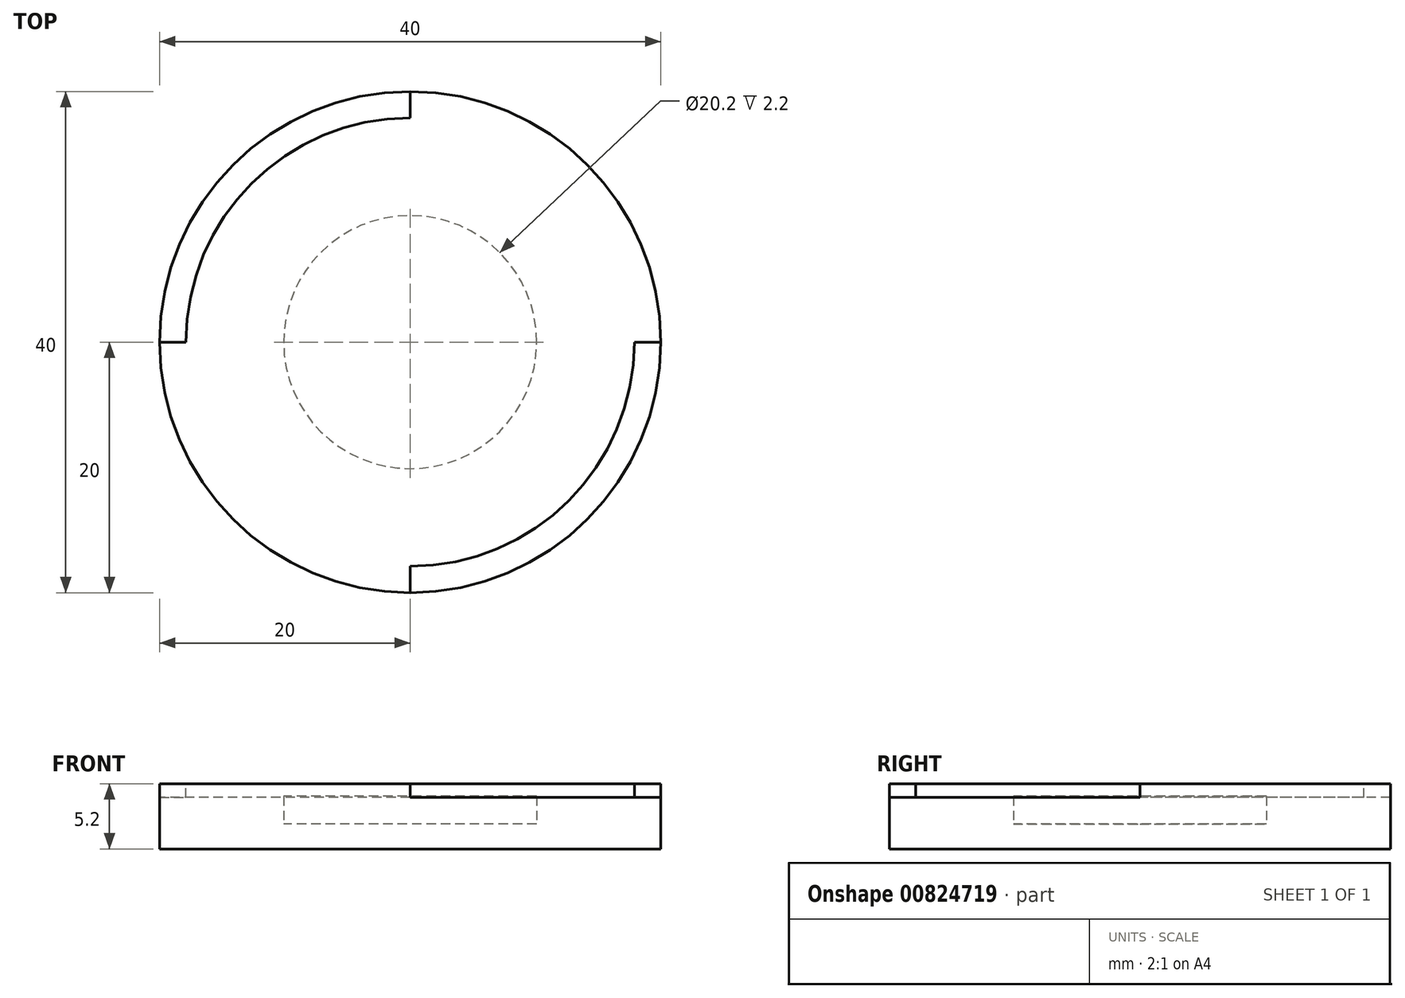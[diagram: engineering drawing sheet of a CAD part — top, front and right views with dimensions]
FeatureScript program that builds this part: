
annotation { "Feature Type Name" : "Feature", "Feature Type Description" : "" }
export const myFeature = defineFeature(function(context is Context, id is Id, definition is map)
    precondition{}
    {
        {
            var Q0;
            Q0=qCreatedBy(makeId("Top.planeOp"),FACE);
            var sketch = newSketch(context, id + "F0", { "sketchPlane" : qUnion([Q0])});
            skCircle(sketch, "E0", {"center": v(0, 0) * mm, "radius": 20 * mm});
            skCircle(sketch, "E1", {"center": v(0, 0) * mm, "radius": 10.1 * mm});
            skSolve(sketch);
        }
        {
            var Q0;
            Q0=makeQuery(id+"F0.imprint","IMPRINT",FACE,{"disambiguationData":[TD([[makeQuery(id+"F0.imprint","IMPRINT",EDGE,{"derivedFrom":sQuery(id+"F0.wireOp",EDGE,"E1")}),1.0]])]});
            var Q1;
            Q1=makeQuery(id+"F0.imprint","IMPRINT",FACE,{"disambiguationData":[TD([[makeQuery(id+"F0.imprint","IMPRINT",EDGE,{"derivedFrom":sQuery(id+"F0.wireOp",EDGE,"E0")}),1.0]])]});
            extrude(context, id + "F1", {"entities" : qUnion([Q0, Q1]), "depth" : 2 * mm, "offsetDistance" : 25 * mm});
        }
        {
            var Q0;
            Q0=makeQuery(id+"F0.imprint","IMPRINT",FACE,{"disambiguationData":[TD([[makeQuery(id+"F0.imprint","IMPRINT",EDGE,{"derivedFrom":sQuery(id+"F0.wireOp",EDGE,"E0")}),1.0]])]});
            extrude(context, id + "F2", {"entities" : qUnion([Q0]), "operationType" : NewBodyOperationType.ADD, "depth" : 4.2 * mm, "offsetDistance" : 25 * mm});
        }
        {
            var Q0;
            Q0=makeQuery(id+"F2.opExtrude","CAP_FACE",FACE,{"disambiguationData":[OSD([sQuery(id+"F0.wireOp",EDGE,"E0"),sQuery(id+"F0.wireOp",EDGE,"E1")])],"isStart":false});
            var sketch = newSketch(context, id + "F3", { "sketchPlane" : qUnion([Q0])});
            skCircle(sketch, "E2.0", {"center": v(0, 0) * mm, "radius": 20 * mm});
            skSolve(sketch);
        }
        {
            var Q0;
            Q0=makeQuery(id+"F3.imprint","IMPRINT",FACE,{"disambiguationData":[TD([[makeQuery(id+"F3.imprint","IMPRINT",EDGE,{"derivedFrom":sQuery(id+"F3.wireOp",EDGE,"E2.0")}),1.0]])]});
            var Q1;
            Q1=makeQuery(id+"F3.imprint","IMPRINT",FACE,{"disambiguationData":[TD([[makeQuery(id+"F3.imprint","IMPRINT",EDGE,{"derivedFrom":makeQuery(id+"F2.opExtrude","CAP_EDGE",EDGE,{"disambiguationData":[OSD([sQuery(id+"F0.wireOp",EDGE,"E1")])],"isStart":false})}),1.0]])]});
            extrude(context, id + "F4", {"entities" : qUnion([Q0, Q1]), "operationType" : NewBodyOperationType.ADD, "depth" : 1 * mm, "offsetDistance" : 25 * mm});
        }
        {
            var Q0;
            Q0=makeQuery(id+"F4.opExtrude","CAP_FACE",FACE,{"disambiguationData":[OSD([sQuery(id+"F3.wireOp",EDGE,"E2.0")])],"isStart":false});
            var sketch = newSketch(context, id + "F5", { "sketchPlane" : qUnion([Q0])});
            skArc(sketch, "E3", {"start": v(-20, 0) * mm, "mid": v(-14.14, 14.14) * mm, "end": v(0, 20) * mm});
            skArc(sketch, "E4", {"start": v(0, -20) * mm, "mid": v(14.14, -14.14) * mm, "end": v(20, 0) * mm});
            skArc(sketch, "E5.0", {"start": v(-17.9, 0) * mm, "mid": v(-12.66, 12.66) * mm, "end": v(0, 17.9) * mm});
            skArc(sketch, "E6.0", {"start": v(0, -17.9) * mm, "mid": v(12.66, -12.66) * mm, "end": v(17.9, 0) * mm});
            skLineSegment(sketch, "E7", {"start": v(0, -17.9) * mm, "end": v(0, -20) * mm});
            skLineSegment(sketch, "E8", {"start": v(17.9, 0) * mm, "end": v(20, 0) * mm});
            skLineSegment(sketch, "E9", {"start": v(0, 20) * mm, "end": v(0, 17.9) * mm});
            skLineSegment(sketch, "E10", {"start": v(-20, 0) * mm, "end": v(-17.9, 0) * mm});
            skSolve(sketch);
        }
        {
            var Q0;
            Q0=makeQuery(id+"F5.imprint","IMPRINT",FACE,{"disambiguationData":[TD([[makeQuery(id+"F5.imprint","IMPRINT",EDGE,{"derivedFrom":sQuery(id+"F5.wireOp",EDGE,"E3")}),1.0]])]});
            var Q1;
            Q1=makeQuery(id+"F5.imprint","IMPRINT",FACE,{"disambiguationData":[TD([[makeQuery(id+"F5.imprint","IMPRINT",EDGE,{"derivedFrom":sQuery(id+"F5.wireOp",EDGE,"E4")}),1.0]])]});
            extrude(context, id + "F6", {"entities" : qUnion([Q0, Q1]), "operationType" : NewBodyOperationType.REMOVE, "depth" : -1.1 * mm, "offsetDistance" : 25 * mm});
        }
    });
